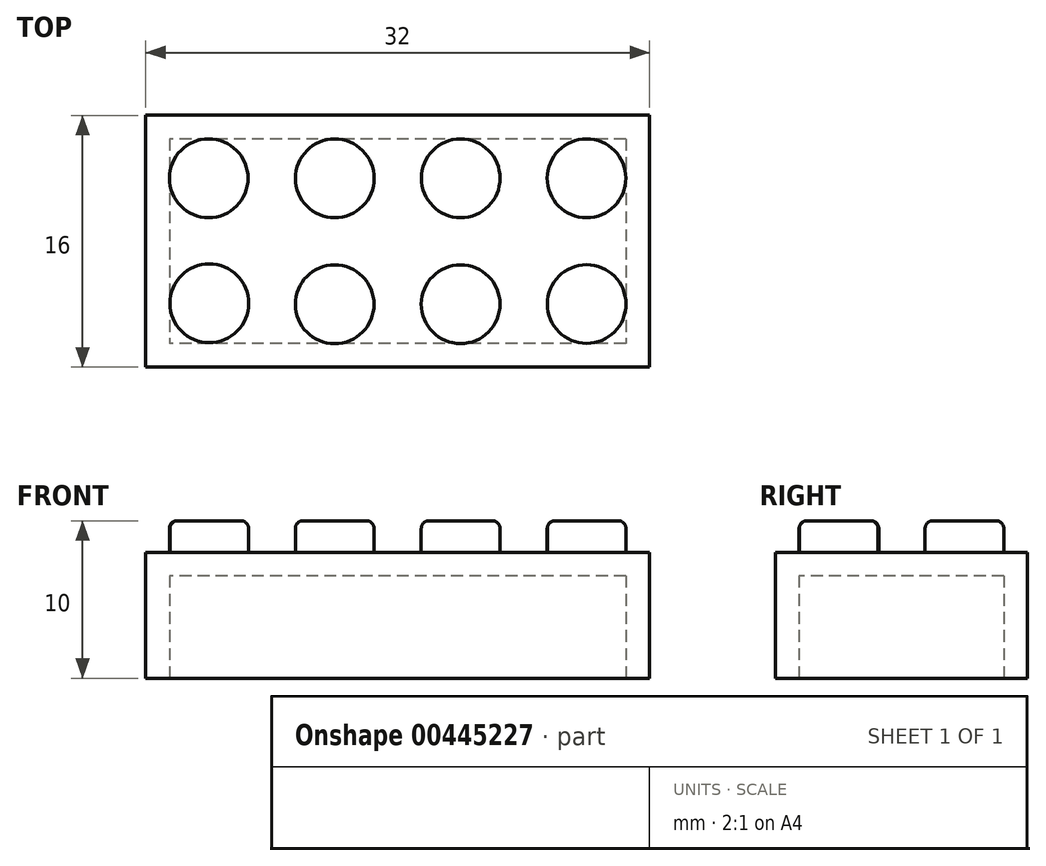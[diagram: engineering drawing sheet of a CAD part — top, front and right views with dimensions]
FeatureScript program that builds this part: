
annotation { "Feature Type Name" : "Feature", "Feature Type Description" : "" }
export const myFeature = defineFeature(function(context is Context, id is Id, definition is map)
    precondition{}
    {
        {
            var Q0;
            Q0=qCreatedBy(makeId("Top.planeOp"),FACE);
            var sketch = newSketch(context, id + "F0", { "sketchPlane" : qUnion([Q0])});
            skLineSegment(sketch, "E0.rect.bottom", {"start": v(-10.92, -30.3) * mm, "end": v(-42.92, -30.3) * mm});
            skLineSegment(sketch, "E0.rect.top", {"start": v(-10.92, -46.3) * mm, "end": v(-42.92, -46.3) * mm});
            skLineSegment(sketch, "E0.rect.left", {"start": v(-10.92, -30.3) * mm, "end": v(-10.92, -46.3) * mm});
            skLineSegment(sketch, "E0.rect.right", {"start": v(-42.92, -30.3) * mm, "end": v(-42.92, -46.3) * mm});
            skPoint(sketch, "E0.rect.middle", {"position": v(-26.92, -38.3) * mm});
            skSolve(sketch);
        }
        {
            var Q0;
            Q0=makeQuery(id+"F0.imprint","IMPRINT",FACE,{"disambiguationData":[TD([[makeQuery(id+"F0.imprint","IMPRINT",EDGE,{"derivedFrom":sQuery(id+"F0.wireOp",EDGE,"E0.rect.bottom")}),1.0]])]});
            extrude(context, id + "F1", {"entities" : qUnion([Q0]), "depth" : 8 * mm});
        }
        {
            var Q0;
            Q0=qCreatedBy(makeId("Top.planeOp"),FACE);
            cPlane(context, id + "F2", {"entities" : qUnion([Q0]), "cplaneType" : CPlaneType.OFFSET, "offset" : 8 * mm, "width" : 150 * mm, "height" : 150 * mm});
        }
        {
            var Q0;
            Q0=makeQuery(id+"F1.opExtrude","CAP_FACE",FACE,{"disambiguationData":[OSD([sQuery(id+"F0.wireOp",EDGE,"E0.rect.bottom"),sQuery(id+"F0.wireOp",EDGE,"E0.rect.top"),sQuery(id+"F0.wireOp",EDGE,"E0.rect.left"),sQuery(id+"F0.wireOp",EDGE,"E0.rect.right")])],"isStart":true});
            shell(context, id + "F3", {"entities" : qUnion([Q0]), "thickness" : 1.5 * mm});
        }
        {
            var Q0;
            Q0=makeQuery(id+"F1.opExtrude","CAP_FACE",FACE,{"disambiguationData":[OSD([sQuery(id+"F0.wireOp",EDGE,"E0.rect.bottom"),sQuery(id+"F0.wireOp",EDGE,"E0.rect.top"),sQuery(id+"F0.wireOp",EDGE,"E0.rect.left"),sQuery(id+"F0.wireOp",EDGE,"E0.rect.right")])],"isStart":false});
            var sketch = newSketch(context, id + "F4", { "sketchPlane" : qUnion([Q0])});
            skCircle(sketch, "E1", {"center": v(-38.92, -34.3) * mm, "radius": 2.5 * mm});
            skCircle(sketch, "E2", {"center": v(-14.92, -42.29) * mm, "radius": 2.5 * mm});
            skCircle(sketch, "E3", {"center": v(-22.92, -42.3) * mm, "radius": 2.5 * mm});
            skCircle(sketch, "E4", {"center": v(-30.91, -34.3) * mm, "radius": 2.5 * mm});
            skCircle(sketch, "E5", {"center": v(-22.92, -34.3) * mm, "radius": 2.5 * mm});
            skCircle(sketch, "E6", {"center": v(-14.92, -34.3) * mm, "radius": 2.5 * mm});
            skCircle(sketch, "E7", {"center": v(-30.92, -42.3) * mm, "radius": 2.5 * mm});
            skCircle(sketch, "E8", {"center": v(-38.88, -42.24) * mm, "radius": 2.5 * mm});
            skLineSegment(sketch, "E9", {"start": v(-42.96, -27.1) * mm, "end": v(-34.96, -27.1) * mm});
            skLineSegment(sketch, "E10", {"start": v(-34.96, -27.1) * mm, "end": v(-26.96, -27.1) * mm});
            skLineSegment(sketch, "E11", {"start": v(-26.96, -27.1) * mm, "end": v(-18.96, -27.1) * mm});
            skLineSegment(sketch, "E12", {"start": v(-18.96, -27.1) * mm, "end": v(-10.96, -27.1) * mm});
            skLineSegment(sketch, "E13", {"start": v(-42.92, -30.3) * mm, "end": v(-42.96, -27.1) * mm});
            skLineSegment(sketch, "E14", {"start": v(-10.92, -30.3) * mm, "end": v(-10.96, -27.1) * mm});
            skLineSegment(sketch, "E15", {"start": v(-34.96, -27.1) * mm, "end": v(-34.96, -49.44) * mm, "construction": true});
            skLineSegment(sketch, "E16", {"start": v(-26.96, -27.1) * mm, "end": v(-26.96, -49.66) * mm, "construction": true});
            skLineSegment(sketch, "E17", {"start": v(-18.96, -27.1) * mm, "end": v(-18.96, -49.44) * mm, "construction": true});
            skLineSegment(sketch, "E18", {"start": v(-42.92, -38.3) * mm, "end": v(-10.92, -38.3) * mm, "construction": true});
            skCircle(sketch, "E19", {"center": v(-34.96, -38.3) * mm, "radius": 3 * mm});
            skCircle(sketch, "E20", {"center": v(-26.96, -38.3) * mm, "radius": 3 * mm});
            skCircle(sketch, "E21", {"center": v(-18.96, -38.3) * mm, "radius": 3 * mm});
            skSolve(sketch);
        }
        {
            var Q0;
            Q0=makeQuery(id+"F4.imprint","IMPRINT",FACE,{"disambiguationData":[TD([[makeQuery(id+"F4.imprint","IMPRINT",EDGE,{"derivedFrom":sQuery(id+"F4.wireOp",EDGE,"E8")}),1.0]])]});
            var Q1;
            Q1=makeQuery(id+"F4.imprint","IMPRINT",FACE,{"disambiguationData":[TD([[makeQuery(id+"F4.imprint","IMPRINT",EDGE,{"derivedFrom":sQuery(id+"F4.wireOp",EDGE,"E7")}),1.0]])]});
            var Q2;
            Q2=makeQuery(id+"F4.imprint","IMPRINT",FACE,{"disambiguationData":[TD([[makeQuery(id+"F4.imprint","IMPRINT",EDGE,{"derivedFrom":sQuery(id+"F4.wireOp",EDGE,"E3")}),1.0]])]});
            var Q3;
            Q3=makeQuery(id+"F4.imprint","IMPRINT",FACE,{"disambiguationData":[TD([[makeQuery(id+"F4.imprint","IMPRINT",EDGE,{"derivedFrom":sQuery(id+"F4.wireOp",EDGE,"E2")}),1.0]])]});
            var Q4;
            Q4=makeQuery(id+"F4.imprint","IMPRINT",FACE,{"disambiguationData":[TD([[makeQuery(id+"F4.imprint","IMPRINT",EDGE,{"derivedFrom":sQuery(id+"F4.wireOp",EDGE,"E1")}),1.0]])]});
            var Q5;
            Q5=makeQuery(id+"F4.imprint","IMPRINT",FACE,{"disambiguationData":[TD([[makeQuery(id+"F4.imprint","IMPRINT",EDGE,{"derivedFrom":sQuery(id+"F4.wireOp",EDGE,"E4")}),1.0]])]});
            var Q6;
            Q6=makeQuery(id+"F4.imprint","IMPRINT",FACE,{"disambiguationData":[TD([[makeQuery(id+"F4.imprint","IMPRINT",EDGE,{"derivedFrom":sQuery(id+"F4.wireOp",EDGE,"E5")}),1.0]])]});
            var Q7;
            Q7=makeQuery(id+"F4.imprint","IMPRINT",FACE,{"disambiguationData":[TD([[makeQuery(id+"F4.imprint","IMPRINT",EDGE,{"derivedFrom":sQuery(id+"F4.wireOp",EDGE,"E6")}),1.0]])]});
            extrude(context, id + "F5", {"entities" : qUnion([Q0, Q1, Q2, Q3, Q4, Q5, Q6, Q7]), "operationType" : NewBodyOperationType.ADD, "depth" : 2 * mm});
        }
        {
            var Q0;
            Q0=makeQuery(id+"F5.opExtrude","CAP_FACE",FACE,{"disambiguationData":[OSD([sQuery(id+"F4.wireOp",EDGE,"E8")])],"isStart":false});
            var Q1;
            Q1=makeQuery(id+"F5.opExtrude","CAP_FACE",FACE,{"disambiguationData":[OSD([sQuery(id+"F4.wireOp",EDGE,"E1")])],"isStart":false});
            var Q2;
            Q2=makeQuery(id+"F5.opExtrude","CAP_FACE",FACE,{"disambiguationData":[OSD([sQuery(id+"F4.wireOp",EDGE,"E7")])],"isStart":false});
            var Q3;
            Q3=makeQuery(id+"F5.opExtrude","CAP_FACE",FACE,{"disambiguationData":[OSD([sQuery(id+"F4.wireOp",EDGE,"E4")])],"isStart":false});
            var Q4;
            Q4=makeQuery(id+"F5.opExtrude","CAP_FACE",FACE,{"disambiguationData":[OSD([sQuery(id+"F4.wireOp",EDGE,"E3")])],"isStart":false});
            var Q5;
            Q5=makeQuery(id+"F5.opExtrude","CAP_FACE",FACE,{"disambiguationData":[OSD([sQuery(id+"F4.wireOp",EDGE,"E5")])],"isStart":false});
            var Q6;
            Q6=makeQuery(id+"F5.opExtrude","CAP_FACE",FACE,{"disambiguationData":[OSD([sQuery(id+"F4.wireOp",EDGE,"E2")])],"isStart":false});
            var Q7;
            Q7=makeQuery(id+"F5.opExtrude","CAP_FACE",FACE,{"disambiguationData":[OSD([sQuery(id+"F4.wireOp",EDGE,"E6")])],"isStart":false});
            fillet(context, id + "F6", {"entities" : qUnion([Q0, Q1, Q2, Q3, Q4, Q5, Q6, Q7]), "radius" : 0.5 * mm, "tangentPropagation" : true, "allowEdgeOverflow" : false});
        }
    });
